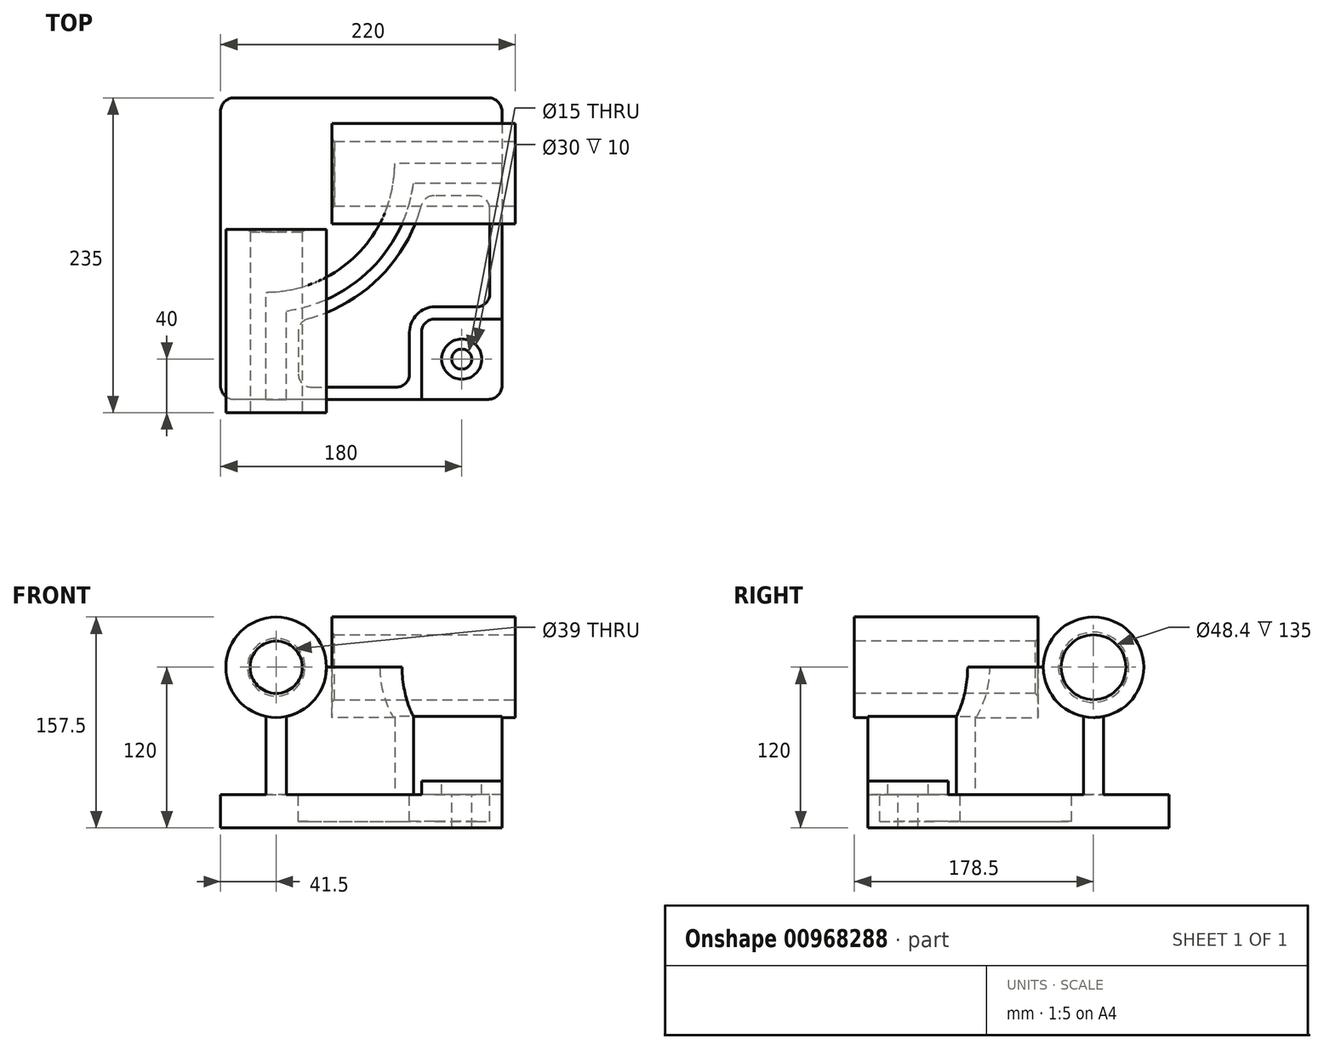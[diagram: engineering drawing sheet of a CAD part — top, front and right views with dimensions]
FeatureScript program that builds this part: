
annotation { "Feature Type Name" : "Feature", "Feature Type Description" : "" }
export const myFeature = defineFeature(function(context is Context, id is Id, definition is map)
    precondition{}
    {
        {
            var Q0;
            Q0=qCreatedBy(makeId("Top.planeOp"),FACE);
            var sketch = newSketch(context, id + "F0", { "sketchPlane" : qUnion([Q0])});
            skLineSegment(sketch, "E0.bottom", {"start": v(105, 112.5) * mm, "end": v(-105, 112.5) * mm});
            skLineSegment(sketch, "E0.top", {"start": v(105, -112.5) * mm, "end": v(-105, -112.5) * mm});
            skLineSegment(sketch, "E0.left", {"start": v(105, 112.5) * mm, "end": v(105, -112.5) * mm});
            skLineSegment(sketch, "E0.right", {"start": v(-105, 112.5) * mm, "end": v(-105, -112.5) * mm});
            skPoint(sketch, "E0.middle", {"position": v(0, 0) * mm});
            skSolve(sketch);
        }
        {
            var Q0;
            Q0=makeQuery(id+"F0.imprint","IMPRINT",FACE,{"disambiguationData":[TD([[makeQuery(id+"F0.imprint","IMPRINT",EDGE,{"derivedFrom":sQuery(id+"F0.wireOp",EDGE,"E0.bottom")}),1.0]])]});
            extrude(context, id + "F1", {"entities" : qUnion([Q0]), "depth" : 25 * mm, "offsetDistance" : 25 * mm});
        }
        {
            var Q0;
            Q0=makeQuery(id+"F1.opExtrude","CAP_FACE",FACE,{"disambiguationData":[OSD([sQuery(id+"F0.wireOp",EDGE,"E0.bottom"),sQuery(id+"F0.wireOp",EDGE,"E0.top"),sQuery(id+"F0.wireOp",EDGE,"E0.left"),sQuery(id+"F0.wireOp",EDGE,"E0.right")])],"isStart":false});
            var sketch = newSketch(context, id + "F2", { "sketchPlane" : qUnion([Q0])});
            skLineSegment(sketch, "E1", {"start": v(-71, -112.5) * mm, "end": v(-71, -32.5) * mm});
            skLineSegment(sketch, "E2", {"start": v(105, 63.5) * mm, "end": v(25, 63.5) * mm});
            skArc(sketch, "E3", {"start": v(-71, -32.5) * mm, "mid": v(-3.12, -4.38) * mm, "end": v(25, 63.5) * mm});
            skLineSegment(sketch, "E4", {"start": v(-71, 63.5) * mm, "end": v(25, 63.5) * mm, "construction": true});
            skLineSegment(sketch, "E5", {"start": v(-71, 63.5) * mm, "end": v(-71, -32.5) * mm, "construction": true});
            skLineSegment(sketch, "E6.0", {"start": v(-56, -112.5) * mm, "end": v(-56, -46.48) * mm});
            skArc(sketch, "E6.1", {"start": v(-56, -46.48) * mm, "mid": v(7.49, -14.99) * mm, "end": v(38.98, 48.5) * mm});
            skLineSegment(sketch, "E6.2", {"start": v(105, 48.5) * mm, "end": v(38.98, 48.5) * mm});
            skLineSegment(sketch, "E7.0", {"start": v(105, 112.5) * mm, "end": v(105, -112.5) * mm});
            skLineSegment(sketch, "E8.0", {"start": v(105, -112.5) * mm, "end": v(-105, -112.5) * mm});
            skSolve(sketch);
        }
        {
            var Q0;
            {var subQ2=sQuery(id+"F2.wireOp",EDGE,"E1");Q0=makeQuery(id+"F2.imprint","IMPRINT",FACE,{"disambiguationData":[TD([[makeQuery(id+"F2.imprint","IMPRINT",EDGE,{"derivedFrom":subQ2}),-1.0]])]});}
            extrude(context, id + "F3", {"entities" : qUnion([Q0]), "operationType" : NewBodyOperationType.ADD, "depth" : 95 * mm, "offsetDistance" : 25 * mm});
        }
        {
            var Q0;
            Q0=makeQuery(id+"F3.boolean.opBoolean","MERGE",FACE,{"derivedFrom":[makeQuery(id+"F1.opExtrude","SWEPT_FACE",FACE,{"disambiguationData":[OSD([sQuery(id+"F0.wireOp",EDGE,"E0.top")])]}),makeQuery(id+"F3.opExtrude","SWEPT_FACE",FACE,{"disambiguationData":[OSD([sQuery(id+"F2.wireOp",EDGE,"E8.0")])]})]});
            var sketch = newSketch(context, id + "F4", { "sketchPlane" : qUnion([Q0])});
            skCircle(sketch, "E9", {"center": v(-63.5, 120) * mm, "radius": 37.5 * mm});
            skSolve(sketch);
        }
        {
            var Q0;
            Q0 = qSketchRegion(id + "F4", true);
            extrude(context, id + "F5", {"entities" : qUnion([Q0]), "operationType" : NewBodyOperationType.ADD, "depth" : 10 * mm, "offsetDistance" : 25 * mm, "hasSecondDirection" : true, "secondDirectionOppositeDirection" : true, "secondDirectionDepth" : (137 - 10) * mm});
        }
        {
            var Q0;
            Q0=makeQuery(id+"F3.boolean.opBoolean","MERGE",FACE,{"derivedFrom":[makeQuery(id+"F1.opExtrude","SWEPT_FACE",FACE,{"disambiguationData":[OSD([sQuery(id+"F0.wireOp",EDGE,"E0.left")])]}),makeQuery(id+"F3.opExtrude","SWEPT_FACE",FACE,{"disambiguationData":[OSD([sQuery(id+"F2.wireOp",EDGE,"E7.0")])]})]});
            var sketch = newSketch(context, id + "F6", { "sketchPlane" : qUnion([Q0])});
            skCircle(sketch, "E10", {"center": v(56, 120) * mm, "radius": 37.5 * mm});
            skSolve(sketch);
        }
        {
            var Q0;
            Q0 = qSketchRegion(id + "F6", true);
            extrude(context, id + "F7", {"entities" : qUnion([Q0]), "operationType" : NewBodyOperationType.ADD, "depth" : 10 * mm, "offsetDistance" : 25 * mm, "hasSecondDirection" : true, "secondDirectionOppositeDirection" : true, "secondDirectionDepth" : (137 - 10) * mm});
        }
        {
            var Q0;
            {var subQ0=sQuery(id+"F0.wireOp",EDGE,"E0.left");var subQ1=sQuery(id+"F0.wireOp",EDGE,"E0.top");Q0=makeQuery(id+"F3.boolean.opBoolean","SPLIT",FACE,{"disambiguationData":[TD([makeQuery(id+"F3.opExtrude","SWEPT_FACE",FACE,{"disambiguationData":[OSD([sQuery(id+"F2.wireOp",EDGE,"E6.0")])]})])],"derivedFrom":makeQuery(id+"F1.opExtrude","CAP_FACE",FACE,{"disambiguationData":[OSD([sQuery(id+"F0.wireOp",EDGE,"E0.bottom"),subQ1,subQ0,sQuery(id+"F0.wireOp",EDGE,"E0.right")])],"isStart":false})});}
            var sketch = newSketch(context, id + "F8", { "sketchPlane" : qUnion([Q0])});
            skLineSegment(sketch, "E11.bottom", {"start": v(105, -112.5) * mm, "end": v(45, -112.5) * mm});
            skLineSegment(sketch, "E11.top", {"start": v(105, -52.5) * mm, "end": v(45, -52.5) * mm});
            skLineSegment(sketch, "E11.left", {"start": v(105, -112.5) * mm, "end": v(105, -52.5) * mm});
            skLineSegment(sketch, "E11.right", {"start": v(45, -112.5) * mm, "end": v(45, -52.5) * mm});
            skSolve(sketch);
        }
        {
            var Q0;
            Q0 = qSketchRegion(id + "F8", true);
            extrude(context, id + "F9", {"entities" : qUnion([Q0]), "operationType" : NewBodyOperationType.ADD, "depth" : (35 - 25) * mm, "offsetDistance" : 25 * mm});
        }
        {
            var Q0;
            Q0=makeQuery(id+"F9.opExtrude","SWEPT_EDGE",EDGE,{"disambiguationData":[OSD([sQuery(id+"F8.wireOp",EDGE,"E11.top"),sQuery(id+"F8.wireOp",EDGE,"E11.right")])]});
            fillet(context, id + "F10", {"entities" : qUnion([Q0]), "radius" : 10 * mm, "tangentPropagation" : true, "allowEdgeOverflow" : false});
        }
        {
            var Q0;
            {var subQ0=sQuery(id+"F0.wireOp",EDGE,"E0.left");var subQ1=sQuery(id+"F0.wireOp",EDGE,"E0.top");Q0=makeQuery(id+"F3.boolean.opBoolean","SPLIT",FACE,{"disambiguationData":[TD([makeQuery(id+"F3.opExtrude","SWEPT_FACE",FACE,{"disambiguationData":[OSD([sQuery(id+"F2.wireOp",EDGE,"E6.0")])]})])],"derivedFrom":makeQuery(id+"F1.opExtrude","CAP_FACE",FACE,{"disambiguationData":[OSD([sQuery(id+"F0.wireOp",EDGE,"E0.bottom"),subQ1,subQ0,sQuery(id+"F0.wireOp",EDGE,"E0.right")])],"isStart":false})});}
            var sketch = newSketch(context, id + "F11", { "sketchPlane" : qUnion([Q0])});
            skLineSegment(sketch, "E12.0", {"start": v(-47, -54.08) * mm, "end": v(-47, -103.5) * mm});
            skArc(sketch, "E12.1", {"start": v(46.58, 39.5) * mm, "mid": v(13.85, -21.35) * mm, "end": v(-47, -54.08) * mm});
            skLineSegment(sketch, "E12.2", {"start": v(-47, -103.5) * mm, "end": v(36, -103.5) * mm});
            skLineSegment(sketch, "E12.3", {"start": v(96, 39.5) * mm, "end": v(46.58, 39.5) * mm});
            skLineSegment(sketch, "E12.4", {"start": v(36, -103.5) * mm, "end": v(36, -62.5) * mm});
            skArc(sketch, "E12.5", {"start": v(36, -62.5) * mm, "mid": v(41.56, -49.06) * mm, "end": v(55, -43.5) * mm});
            skLineSegment(sketch, "E12.6", {"start": v(55, -43.5) * mm, "end": v(96, -43.5) * mm});
            skLineSegment(sketch, "E12.7", {"start": v(96, -43.5) * mm, "end": v(96, 39.5) * mm});
            skSolve(sketch);
        }
        {
            var Q0;
            Q0 = qSketchRegion(id + "F11", true);
            extrude(context, id + "F12", {"entities" : qUnion([Q0]), "operationType" : NewBodyOperationType.REMOVE, "oppositeDirection" : true, "depth" : (25 - 5) * mm, "offsetDistance" : 25 * mm});
        }
        {
            var Q0;
            Q0=makeQuery(id+"F9.opExtrude","CAP_FACE",FACE,{"disambiguationData":[OSD([sQuery(id+"F8.wireOp",EDGE,"E11.bottom"),sQuery(id+"F8.wireOp",EDGE,"E11.top"),sQuery(id+"F8.wireOp",EDGE,"E11.left"),sQuery(id+"F8.wireOp",EDGE,"E11.right")])],"isStart":false});
            var sketch = newSketch(context, id + "F13", { "sketchPlane" : qUnion([Q0])});
            skCircle(sketch, "E13", {"center": v(75, -82.5) * mm, "radius": 15 * mm});
            skSolve(sketch);
        }
        {
            var Q0;
            Q0=sQuery(id+"F13.wireOp",VERTEX,"E13.center");
            var Q1;
            Q1=makeQuery(id+"F1.opExtrude","SWEPT_BODY",BODY,{"disambiguationData":[OSD([sQuery(id+"F0.wireOp",EDGE,"E0.bottom"),sQuery(id+"F0.wireOp",EDGE,"E0.top"),sQuery(id+"F0.wireOp",EDGE,"E0.left"),sQuery(id+"F0.wireOp",EDGE,"E0.right")])]});
            hole(context, id + "F14", {"style" : HoleStyle.C_BORE, "endStyle" : HoleEndStyle.THROUGH, "holeDiameter" : 15 * mm, "cBoreDiameter" : 30 * mm, "cBoreDepth" : 10 * mm, "majorDiameter" : 5 * mm, "isTappedThrough" : true, "tappedDepth" : 12 * mm, "tapClearance" : 3, "locations" : qUnion([Q0]), "scope" : qUnion([Q1])});
        }
        {
            var Q0;
            Q0=makeQuery(id+"F12.boolean.opBoolean","COPY",EDGE,{"derivedFrom":makeQuery(id+"F12.opExtrude","SWEPT_EDGE",EDGE,{"disambiguationData":[OSD([sQuery(id+"F11.wireOp",EDGE,"E12.1"),sQuery(id+"F11.wireOp",EDGE,"E12.3")])]})});
            var Q1;
            Q1=makeQuery(id+"F12.boolean.opBoolean","COPY",EDGE,{"derivedFrom":makeQuery(id+"F12.opExtrude","SWEPT_EDGE",EDGE,{"disambiguationData":[OSD([sQuery(id+"F11.wireOp",EDGE,"E12.0"),sQuery(id+"F11.wireOp",EDGE,"E12.1")])]})});
            var Q2;
            Q2=makeQuery(id+"F12.boolean.opBoolean","COPY",EDGE,{"derivedFrom":makeQuery(id+"F12.opExtrude","SWEPT_EDGE",EDGE,{"disambiguationData":[OSD([sQuery(id+"F11.wireOp",EDGE,"E12.0"),sQuery(id+"F11.wireOp",EDGE,"E12.2")])]})});
            var Q3;
            Q3=makeQuery(id+"F12.boolean.opBoolean","COPY",EDGE,{"derivedFrom":makeQuery(id+"F12.opExtrude","SWEPT_EDGE",EDGE,{"disambiguationData":[OSD([sQuery(id+"F11.wireOp",EDGE,"E12.3"),sQuery(id+"F11.wireOp",EDGE,"E12.7")])]})});
            var Q4;
            Q4=makeQuery(id+"F12.boolean.opBoolean","COPY",EDGE,{"derivedFrom":makeQuery(id+"F12.opExtrude","SWEPT_EDGE",EDGE,{"disambiguationData":[OSD([sQuery(id+"F11.wireOp",EDGE,"E12.6"),sQuery(id+"F11.wireOp",EDGE,"E12.7")])]})});
            var Q5;
            Q5=makeQuery(id+"F12.boolean.opBoolean","COPY",EDGE,{"derivedFrom":makeQuery(id+"F12.opExtrude","SWEPT_EDGE",EDGE,{"disambiguationData":[OSD([sQuery(id+"F11.wireOp",EDGE,"E12.2"),sQuery(id+"F11.wireOp",EDGE,"E12.4")])]})});
            fillet(context, id + "F15", {"entities" : qUnion([Q0, Q1, Q2, Q3, Q4, Q5]), "radius" : 10 * mm, "tangentPropagation" : true, "allowEdgeOverflow" : false});
        }
        {
            var Q0;
            Q0=makeQuery(id+"F5.opExtrude","CAP_FACE",FACE,{"disambiguationData":[OSD([sQuery(id+"F4.wireOp",EDGE,"E9")])],"isStart":false});
            var sketch = newSketch(context, id + "F16", { "sketchPlane" : qUnion([Q0])});
            skCircle(sketch, "E14", {"center": v(-63.5, 120) * mm, "radius": 19.5 * mm});
            skSolve(sketch);
        }
        {
            var Q0;
            Q0 = qSketchRegion(id + "F16", true);
            extrude(context, id + "F17", {"entities" : qUnion([Q0]), "operationType" : NewBodyOperationType.REMOVE, "endBound" : BoundingType.THROUGH_ALL, "oppositeDirection" : true, "depth" : 25 * mm, "offsetDistance" : 25 * mm});
        }
        {
            var Q0;
            Q0=makeQuery(id+"F7.opExtrude","CAP_FACE",FACE,{"disambiguationData":[OSD([sQuery(id+"F6.wireOp",EDGE,"E10")])],"isStart":false});
            var sketch = newSketch(context, id + "F18", { "sketchPlane" : qUnion([Q0])});
            skCircle(sketch, "E15", {"center": v(56, 120) * mm, "radius": 24.2 * mm});
            skSolve(sketch);
        }
        {
            var Q0;
            Q0=makeQuery(id+"F18.imprint","IMPRINT",FACE,{"disambiguationData":[TD([[makeQuery(id+"F18.imprint","IMPRINT",EDGE,{"derivedFrom":sQuery(id+"F18.wireOp",EDGE,"E15")}),1.0]])]});
            extrude(context, id + "F19", {"entities" : qUnion([Q0]), "operationType" : NewBodyOperationType.REMOVE, "endBound" : BoundingType.THROUGH_ALL, "oppositeDirection" : true, "depth" : 25 * mm, "offsetDistance" : 25 * mm});
        }
        {
            var Q0;
            Q0=makeQuery(id+"F17.boolean.opBoolean","COPY",EDGE,{"derivedFrom":makeQuery(id+"F17.opExtrude","CAP_EDGE",EDGE,{"disambiguationData":[OSD([sQuery(id+"F16.wireOp",EDGE,"E14")])],"isStart":true})});
            var Q1;
            Q1=makeQuery(id+"F19.boolean.opBoolean","COPY",EDGE,{"derivedFrom":makeQuery(id+"F19.opExtrude","CAP_EDGE",EDGE,{"disambiguationData":[OSD([sQuery(id+"F18.wireOp",EDGE,"E15")])],"isStart":true})});
            var Q2;
            Q2=makeQuery(id+"F19.boolean.opBoolean","INTERSECT",EDGE,{"derivedFrom":[makeQuery(id+"F7.opExtrude","CAP_FACE",FACE,{"disambiguationData":[OSD([sQuery(id+"F6.wireOp",EDGE,"E10")])],"isStart":true}),makeQuery(id+"F19.opExtrude","SWEPT_FACE",FACE,{"disambiguationData":[OSD([sQuery(id+"F18.wireOp",EDGE,"E15")])]})]});
            var Q3;
            Q3=makeQuery(id+"F17.boolean.opBoolean","INTERSECT",EDGE,{"derivedFrom":[makeQuery(id+"F5.opExtrude","CAP_FACE",FACE,{"disambiguationData":[OSD([sQuery(id+"F4.wireOp",EDGE,"E9")])],"isStart":true}),makeQuery(id+"F17.opExtrude","SWEPT_FACE",FACE,{"disambiguationData":[OSD([sQuery(id+"F16.wireOp",EDGE,"E14")])]})]});
            chamfer(context, id + "F20", {"entities" : qUnion([Q0, Q1, Q2, Q3]), "width" : 2 * mm, "tangentPropagation" : true});
        }
        {
            var Q0;
            Q0=makeQuery(id+"F1.opExtrude","SWEPT_EDGE",EDGE,{"disambiguationData":[OSD([sQuery(id+"F0.wireOp",EDGE,"E0.top"),sQuery(id+"F0.wireOp",EDGE,"E0.right")])]});
            var Q1;
            Q1=makeQuery(id+"F9.boolean.opBoolean","MERGE",EDGE,{"derivedFrom":[makeQuery(id+"F1.opExtrude","SWEPT_EDGE",EDGE,{"disambiguationData":[OSD([sQuery(id+"F0.wireOp",EDGE,"E0.top"),sQuery(id+"F0.wireOp",EDGE,"E0.left")])]}),makeQuery(id+"F9.opExtrude","SWEPT_EDGE",EDGE,{"disambiguationData":[OSD([sQuery(id+"F8.wireOp",EDGE,"E11.bottom"),sQuery(id+"F8.wireOp",EDGE,"E11.left")])]})]});
            var Q2;
            Q2=makeQuery(id+"F1.opExtrude","SWEPT_EDGE",EDGE,{"disambiguationData":[OSD([sQuery(id+"F0.wireOp",EDGE,"E0.bottom"),sQuery(id+"F0.wireOp",EDGE,"E0.left")])]});
            var Q3;
            Q3=makeQuery(id+"F1.opExtrude","SWEPT_EDGE",EDGE,{"disambiguationData":[OSD([sQuery(id+"F0.wireOp",EDGE,"E0.bottom"),sQuery(id+"F0.wireOp",EDGE,"E0.right")])]});
            fillet(context, id + "F21", {"entities" : qUnion([Q0, Q1, Q2, Q3]), "radius" : 10 * mm, "tangentPropagation" : true, "allowEdgeOverflow" : false});
        }
    });
